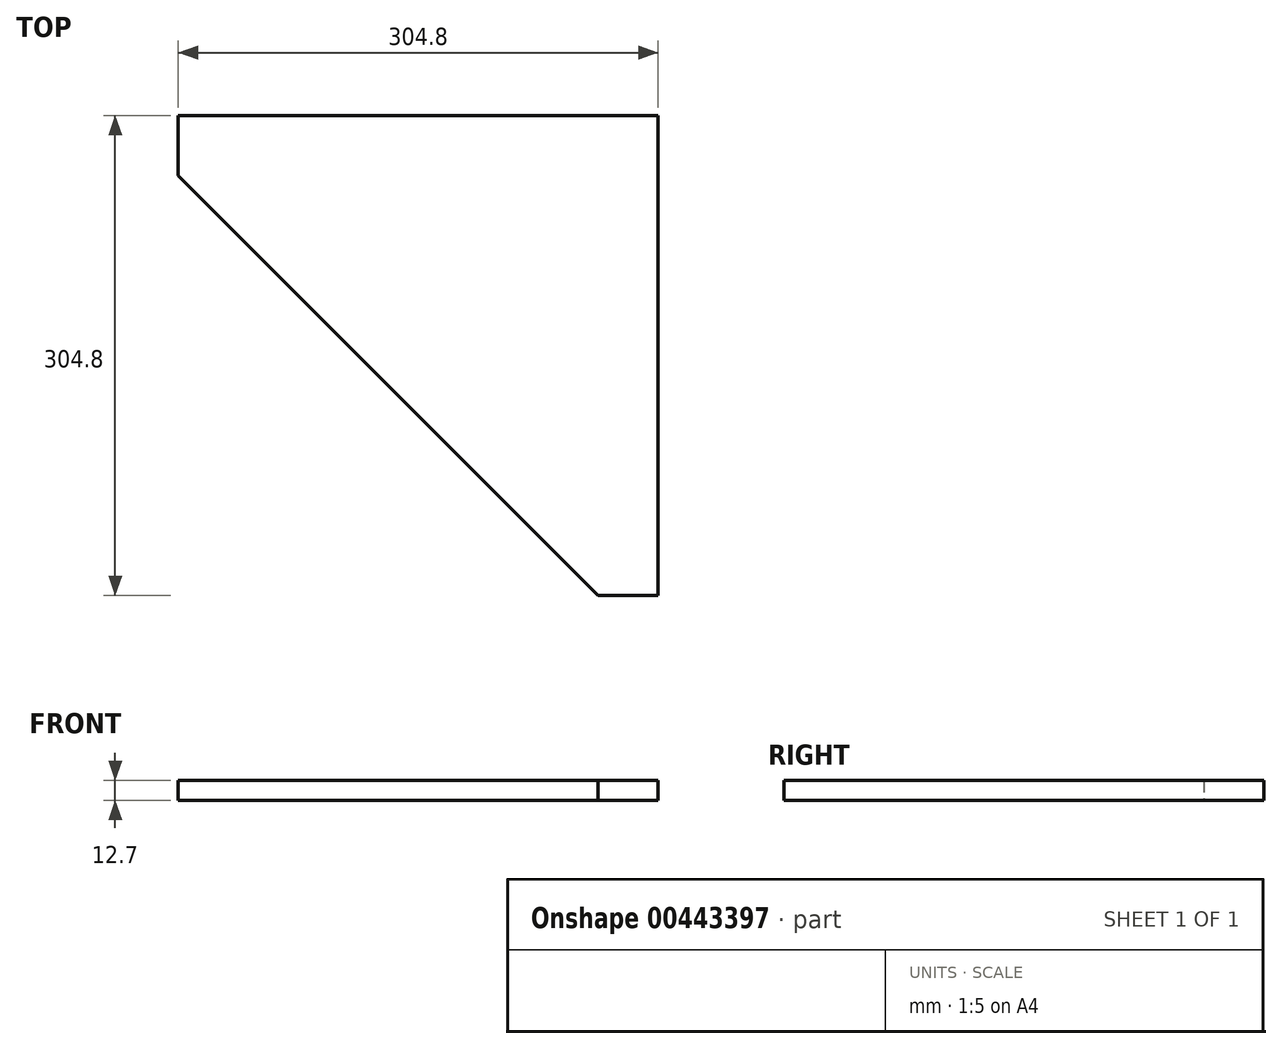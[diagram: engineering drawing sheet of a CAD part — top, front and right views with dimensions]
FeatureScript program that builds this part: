
annotation { "Feature Type Name" : "Feature", "Feature Type Description" : "" }
export const myFeature = defineFeature(function(context is Context, id is Id, definition is map)
    precondition{}
    {
        {
            var Q0;
            Q0=qCreatedBy(makeId("Top.planeOp"),FACE);
            var sketch = newSketch(context, id + "F0", { "sketchPlane" : qUnion([Q0])});
            skLineSegment(sketch, "E0", {"start": v(-149.27, 177.6) * mm, "end": v(155.53, 177.6) * mm});
            skLineSegment(sketch, "E1", {"start": v(155.53, 177.6) * mm, "end": v(155.53, -127.2) * mm});
            skLineSegment(sketch, "E2", {"start": v(-149.27, 177.6) * mm, "end": v(-149.27, 139.5) * mm});
            skLineSegment(sketch, "E3", {"start": v(155.53, -127.2) * mm, "end": v(117.43, -127.2) * mm});
            skLineSegment(sketch, "E4", {"start": v(-149.27, 139.5) * mm, "end": v(117.43, -127.2) * mm});
            skSolve(sketch);
        }
        {
            var Q0;
            Q0 = qSketchRegion(id + "F0", true);
            extrude(context, id + "F1", {"entities" : qUnion([Q0]), "depth" : 12.7 * mm});
        }
    });
